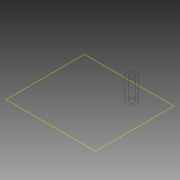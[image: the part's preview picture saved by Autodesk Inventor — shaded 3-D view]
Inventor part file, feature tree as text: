
AUTODESK INVENTOR PART (.ipt)
format: ipt  version: 2015 (Build 190159000, 159)  size: 78,336 bytes
history: native  units: mm
features: plane x2, extrude x1
ambient origin geometry x8: Origin, YZ Plane, XZ Plane, XY Plane, X Axis, Y Axis, Z Axis, Center Point
bodies: Solid1 (feature_tree)
feature tree (3):
  plane  "Work Plane1"
  plane  "Work Plane2"
  extrude  "Extrusion1"  Depth=10.0mm
